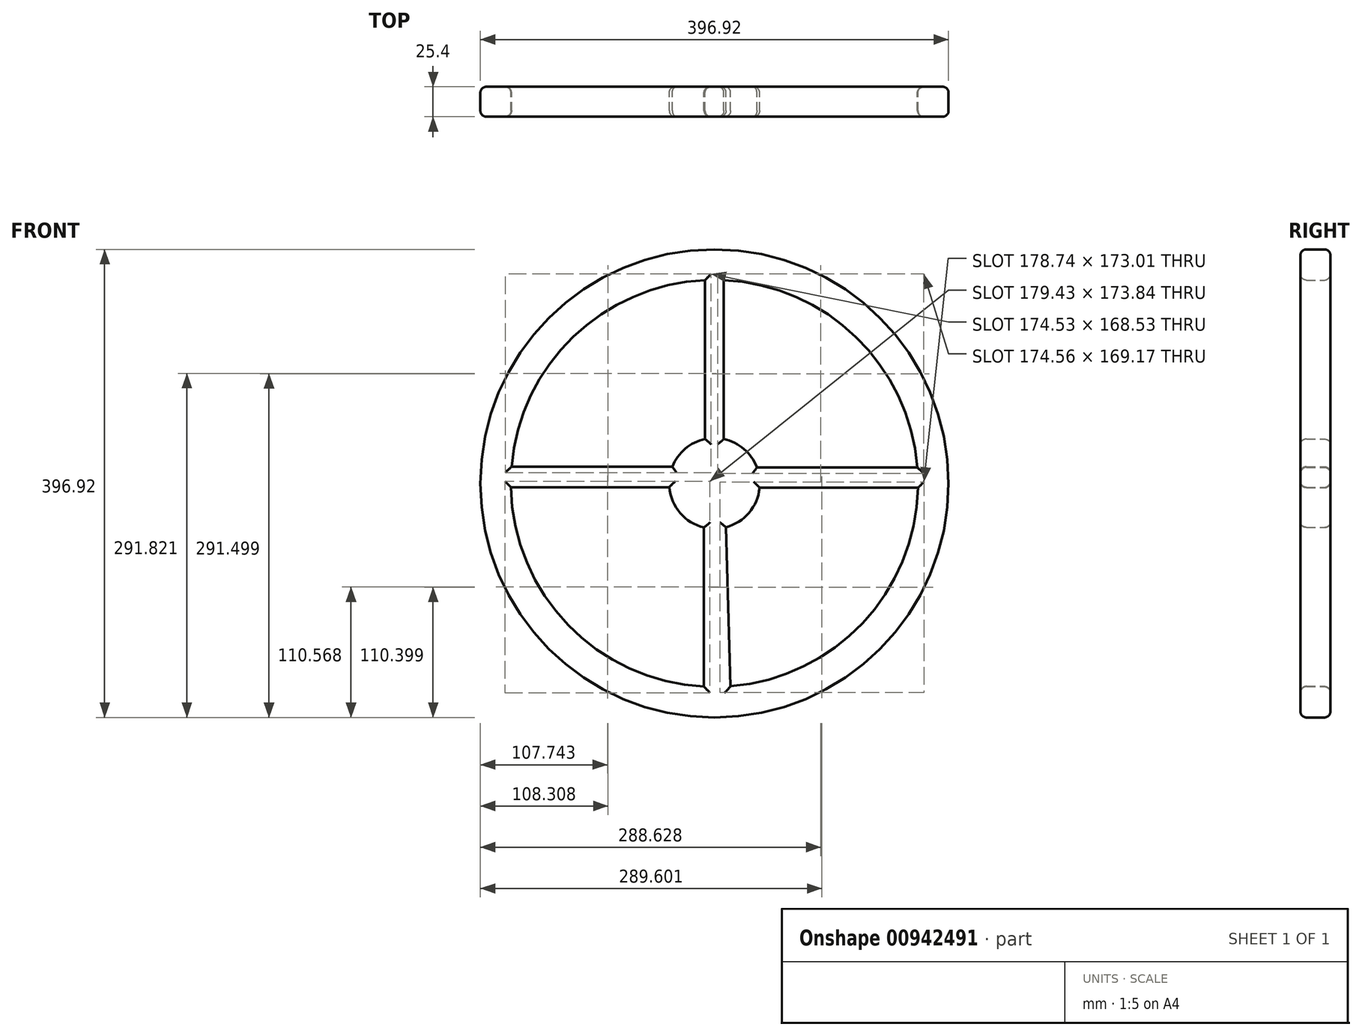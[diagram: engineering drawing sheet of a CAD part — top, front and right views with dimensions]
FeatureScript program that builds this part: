
annotation { "Feature Type Name" : "Feature", "Feature Type Description" : "" }
export const myFeature = defineFeature(function(context is Context, id is Id, definition is map)
    precondition{}
    {
        {
            var Q0;
            Q0=qCreatedBy(makeId("Front.planeOp"),FACE);
            var sketch = newSketch(context, id + "F0", { "sketchPlane" : qUnion([Q0])});
            skCircle(sketch, "E0", {"center": v(0, 0) * mm, "radius": 198.46 * mm});
            skCircle(sketch, "E1", {"center": v(0, 0) * mm, "radius": 172.57 * mm});
            skCircle(sketch, "E2", {"center": v(0, 0) * mm, "radius": 38.43 * mm});
            skLineSegment(sketch, "E3", {"start": v(-7.97, 172.38) * mm, "end": v(-7.97, 37.6) * mm});
            skLineSegment(sketch, "E4", {"start": v(7.97, 37.6) * mm, "end": v(7.97, 172.38) * mm});
            skLineSegment(sketch, "E5", {"start": v(-8.87, -37.4) * mm, "end": v(-8.87, -172.34) * mm});
            skLineSegment(sketch, "E6", {"start": v(9.84, -37.15) * mm, "end": v(13.69, -172.02) * mm});
            skLineSegment(sketch, "E7", {"start": v(-35.72, 14.18) * mm, "end": v(-171.98, 14.18) * mm});
            skLineSegment(sketch, "E8", {"start": v(-38.3, -3.26) * mm, "end": v(-172.54, -3.26) * mm});
            skLineSegment(sketch, "E9", {"start": v(35.97, 13.53) * mm, "end": v(172.04, 13.53) * mm});
            skLineSegment(sketch, "E10", {"start": v(38.24, -3.77) * mm, "end": v(172.53, -3.77) * mm});
            skSolve(sketch);
        }
        {
            var Q0;
            Q0=makeQuery(id+"F0.imprint","IMPRINT",FACE,{"disambiguationData":[TD([[makeQuery(id+"F0.imprint","IMPRINT",EDGE,{"derivedFrom":sQuery(id+"F0.wireOp",EDGE,"E0")}),1.0]])]});
            var Q1;
            {var subQ0=sQuery(id+"F0.wireOp",EDGE,"E3");Q1=makeQuery(id+"F0.imprint","IMPRINT",FACE,{"disambiguationData":[TD([[makeQuery(id+"F0.imprint","IMPRINT",EDGE,{"derivedFrom":subQ0}),1.0]])]});}
            var Q2;
            {var subQ0=sQuery(id+"F0.wireOp",EDGE,"E7");Q2=makeQuery(id+"F0.imprint","IMPRINT",FACE,{"disambiguationData":[TD([[makeQuery(id+"F0.imprint","IMPRINT",EDGE,{"derivedFrom":subQ0}),1.0]])]});}
            var Q3;
            {var subQ4=sQuery(id+"F0.wireOp",EDGE,"DAilxVQu-HEWN-SxXB-gtyP-NfDb4dbdtztd");Q3=makeQuery(id+"F0.imprint","IMPRINT",FACE,{"disambiguationData":[TD([[makeQuery(id+"F0.imprint","IMPRINT",EDGE,{"derivedFrom":subQ4}),-1.0]])]});}
            var Q4;
            {var subQ0=sQuery(id+"F0.wireOp",EDGE,"E9");Q4=makeQuery(id+"F0.imprint","IMPRINT",FACE,{"disambiguationData":[TD([[makeQuery(id+"F0.imprint","IMPRINT",EDGE,{"derivedFrom":subQ0}),-1.0]])]});}
            var Q5;
            {var subQ0=sQuery(id+"F0.wireOp",EDGE,"E5");Q5=makeQuery(id+"F0.imprint","IMPRINT",FACE,{"disambiguationData":[TD([[makeQuery(id+"F0.imprint","IMPRINT",EDGE,{"derivedFrom":subQ0}),1.0]])]});}
            var Q6;
            {var subQ0=sQuery(id+"F0.wireOp",EDGE,"E2");var subQ4=makeQuery(id+"F0.imprint","INTERSECT",VERTEX,{"derivedFrom":[subQ0,sQuery(id+"F0.wireOp",EDGE,"E4")]});Q6=makeQuery(id+"F0.imprint","IMPRINT",FACE,{"disambiguationData":[TD([[makeQuery(id+"F0.imprint","IMPRINT",EDGE,{"disambiguationData":[TD([[subQ4,1.0]])],"derivedFrom":subQ0}),1.0]])]});}
            extrude(context, id + "F1", {"entities" : qUnion([Q0, Q1, Q2, Q3, Q4, Q5, Q6]), "depth" : 25.4 * mm, "offsetDistance" : 25.4 * mm});
        }
        {
            var Q0;
            Q0=makeQuery(id+"F1.opExtrude","CAP_EDGE",EDGE,{"disambiguationData":[OSD([sQuery(id+"F0.wireOp",EDGE,"E0")])],"isStart":false});
            var Q1;
            {var subQ0=sQuery(id+"F0.wireOp",EDGE,"E1");Q1=makeQuery(id+"F1.opExtrude","CAP_EDGE",EDGE,{"disambiguationData":[OSD([subQ0]),TDD([makeQuery(id+"F0.imprint","IMPRINT",EDGE,{"disambiguationData":[TD([[makeQuery(id+"F0.imprint","INTERSECT",VERTEX,{"derivedFrom":[subQ0,sQuery(id+"F0.wireOp",EDGE,"E3")]}),-1.0]])],"derivedFrom":subQ0})])],"isStart":false});}
            var Q2;
            {var subQ0=sQuery(id+"F0.wireOp",EDGE,"E1");Q2=makeQuery(id+"F1.opExtrude","CAP_EDGE",EDGE,{"disambiguationData":[OSD([subQ0]),TDD([makeQuery(id+"F0.imprint","IMPRINT",EDGE,{"disambiguationData":[TD([[makeQuery(id+"F0.imprint","INTERSECT",VERTEX,{"derivedFrom":[subQ0,sQuery(id+"F0.wireOp",EDGE,"E4")]}),1.0]])],"derivedFrom":subQ0})])],"isStart":false});}
            var Q3;
            {var subQ0=sQuery(id+"F0.wireOp",EDGE,"E1");Q3=makeQuery(id+"F1.opExtrude","CAP_EDGE",EDGE,{"disambiguationData":[OSD([subQ0]),TDD([makeQuery(id+"F0.imprint","IMPRINT",EDGE,{"disambiguationData":[TD([[makeQuery(id+"F0.imprint","INTERSECT",VERTEX,{"derivedFrom":[subQ0,sQuery(id+"F0.wireOp",EDGE,"E6")]}),-1.0]])],"derivedFrom":subQ0})])],"isStart":false});}
            var Q4;
            {var subQ0=sQuery(id+"F0.wireOp",EDGE,"E1");Q4=makeQuery(id+"F1.opExtrude","CAP_EDGE",EDGE,{"disambiguationData":[OSD([subQ0]),TDD([makeQuery(id+"F0.imprint","IMPRINT",EDGE,{"disambiguationData":[TD([[makeQuery(id+"F0.imprint","INTERSECT",VERTEX,{"derivedFrom":[subQ0,sQuery(id+"F0.wireOp",EDGE,"E5")]}),1.0]])],"derivedFrom":subQ0})])],"isStart":false});}
            fillet(context, id + "F2", {"entities" : qUnion([Q0, Q1, Q2, Q3, Q4]), "radius" : 5.08 * mm, "tangentPropagation" : true, "allowEdgeOverflow" : false});
        }
        {
            var Q0;
            Q0=makeQuery(id+"F1.opExtrude","CAP_EDGE",EDGE,{"disambiguationData":[OSD([sQuery(id+"F0.wireOp",EDGE,"E0")])],"isStart":true});
            var Q1;
            {var subQ0=sQuery(id+"F0.wireOp",EDGE,"E1");Q1=makeQuery(id+"F1.opExtrude","CAP_EDGE",EDGE,{"disambiguationData":[OSD([subQ0]),TDD([makeQuery(id+"F0.imprint","IMPRINT",EDGE,{"disambiguationData":[TD([[makeQuery(id+"F0.imprint","INTERSECT",VERTEX,{"derivedFrom":[subQ0,sQuery(id+"F0.wireOp",EDGE,"E4")]}),1.0]])],"derivedFrom":subQ0})])],"isStart":true});}
            var Q2;
            {var subQ0=sQuery(id+"F0.wireOp",EDGE,"E1");Q2=makeQuery(id+"F1.opExtrude","CAP_EDGE",EDGE,{"disambiguationData":[OSD([subQ0]),TDD([makeQuery(id+"F0.imprint","IMPRINT",EDGE,{"disambiguationData":[TD([[makeQuery(id+"F0.imprint","INTERSECT",VERTEX,{"derivedFrom":[subQ0,sQuery(id+"F0.wireOp",EDGE,"E6")]}),-1.0]])],"derivedFrom":subQ0})])],"isStart":true});}
            var Q3;
            {var subQ0=sQuery(id+"F0.wireOp",EDGE,"E1");Q3=makeQuery(id+"F1.opExtrude","CAP_EDGE",EDGE,{"disambiguationData":[OSD([subQ0]),TDD([makeQuery(id+"F0.imprint","IMPRINT",EDGE,{"disambiguationData":[TD([[makeQuery(id+"F0.imprint","INTERSECT",VERTEX,{"derivedFrom":[subQ0,sQuery(id+"F0.wireOp",EDGE,"E3")]}),-1.0]])],"derivedFrom":subQ0})])],"isStart":true});}
            var Q4;
            {var subQ0=sQuery(id+"F0.wireOp",EDGE,"E1");Q4=makeQuery(id+"F1.opExtrude","CAP_EDGE",EDGE,{"disambiguationData":[OSD([subQ0]),TDD([makeQuery(id+"F0.imprint","IMPRINT",EDGE,{"disambiguationData":[TD([[makeQuery(id+"F0.imprint","INTERSECT",VERTEX,{"derivedFrom":[subQ0,sQuery(id+"F0.wireOp",EDGE,"E5")]}),1.0]])],"derivedFrom":subQ0})])],"isStart":true});}
            fillet(context, id + "F3", {"entities" : qUnion([Q0, Q1, Q2, Q3, Q4]), "radius" : 5.08 * mm, "tangentPropagation" : true, "allowEdgeOverflow" : false});
        }
        {
            var Q0;
            Q0=makeQuery(id+"F1.opExtrude","CAP_EDGE",EDGE,{"disambiguationData":[OSD([sQuery(id+"F0.wireOp",EDGE,"E3")])],"isStart":true});
            var Q1;
            Q1=makeQuery(id+"F1.opExtrude","CAP_EDGE",EDGE,{"disambiguationData":[OSD([sQuery(id+"F0.wireOp",EDGE,"E4")])],"isStart":false});
            var Q2;
            Q2=makeQuery(id+"F1.opExtrude","CAP_EDGE",EDGE,{"disambiguationData":[OSD([sQuery(id+"F0.wireOp",EDGE,"E4")])],"isStart":true});
            var Q3;
            Q3=makeQuery(id+"F1.opExtrude","CAP_EDGE",EDGE,{"disambiguationData":[OSD([sQuery(id+"F0.wireOp",EDGE,"E3")])],"isStart":false});
            fillet(context, id + "F4", {"entities" : qUnion([Q0, Q1, Q2, Q3]), "radius" : 5.08 * mm, "tangentPropagation" : true, "allowEdgeOverflow" : false});
        }
        {
            var Q0;
            Q0=makeQuery(id+"F1.opExtrude","CAP_EDGE",EDGE,{"disambiguationData":[OSD([sQuery(id+"F0.wireOp",EDGE,"E10")])],"isStart":true});
            var Q1;
            Q1=makeQuery(id+"F1.opExtrude","CAP_EDGE",EDGE,{"disambiguationData":[OSD([sQuery(id+"F0.wireOp",EDGE,"E9")])],"isStart":true});
            var Q2;
            Q2=makeQuery(id+"F1.opExtrude","CAP_EDGE",EDGE,{"disambiguationData":[OSD([sQuery(id+"F0.wireOp",EDGE,"E9")])],"isStart":false});
            var Q3;
            Q3=makeQuery(id+"F1.opExtrude","CAP_EDGE",EDGE,{"disambiguationData":[OSD([sQuery(id+"F0.wireOp",EDGE,"E10")])],"isStart":false});
            fillet(context, id + "F5", {"entities" : qUnion([Q0, Q1, Q2, Q3]), "radius" : 5.08 * mm, "tangentPropagation" : true, "allowEdgeOverflow" : false});
        }
        {
            var Q0;
            Q0=makeQuery(id+"F1.opExtrude","CAP_EDGE",EDGE,{"disambiguationData":[OSD([sQuery(id+"F0.wireOp",EDGE,"E6")])],"isStart":true});
            var Q1;
            Q1=makeQuery(id+"F1.opExtrude","CAP_EDGE",EDGE,{"disambiguationData":[OSD([sQuery(id+"F0.wireOp",EDGE,"E5")])],"isStart":true});
            var Q2;
            Q2=makeQuery(id+"F1.opExtrude","CAP_EDGE",EDGE,{"disambiguationData":[OSD([sQuery(id+"F0.wireOp",EDGE,"E6")])],"isStart":false});
            var Q3;
            Q3=makeQuery(id+"F1.opExtrude","CAP_EDGE",EDGE,{"disambiguationData":[OSD([sQuery(id+"F0.wireOp",EDGE,"E5")])],"isStart":false});
            fillet(context, id + "F6", {"entities" : qUnion([Q0, Q1, Q2, Q3]), "radius" : 5.08 * mm, "tangentPropagation" : true, "allowEdgeOverflow" : false});
        }
        {
            var Q0;
            Q0=makeQuery(id+"F1.opExtrude","CAP_EDGE",EDGE,{"disambiguationData":[OSD([sQuery(id+"F0.wireOp",EDGE,"E7")])],"isStart":false});
            var Q1;
            Q1=makeQuery(id+"F1.opExtrude","CAP_EDGE",EDGE,{"disambiguationData":[OSD([sQuery(id+"F0.wireOp",EDGE,"E8")])],"isStart":false});
            var Q2;
            Q2=makeQuery(id+"F1.opExtrude","CAP_EDGE",EDGE,{"disambiguationData":[OSD([sQuery(id+"F0.wireOp",EDGE,"E8")])],"isStart":true});
            var Q3;
            Q3=makeQuery(id+"F1.opExtrude","CAP_EDGE",EDGE,{"disambiguationData":[OSD([sQuery(id+"F0.wireOp",EDGE,"E7")])],"isStart":true});
            fillet(context, id + "F7", {"entities" : qUnion([Q0, Q1, Q2, Q3]), "radius" : 5.08 * mm, "tangentPropagation" : true, "allowEdgeOverflow" : false});
        }
        {
            var Q0;
            {var subQ0=sQuery(id+"F0.wireOp",EDGE,"E2");Q0=makeQuery(id+"F1.opExtrude","CAP_EDGE",EDGE,{"disambiguationData":[OSD([subQ0]),TDD([makeQuery(id+"F0.imprint","IMPRINT",EDGE,{"disambiguationData":[TD([[makeQuery(id+"F0.imprint","INTERSECT",VERTEX,{"derivedFrom":[subQ0,sQuery(id+"F0.wireOp",EDGE,"E4")]}),1.0]])],"derivedFrom":subQ0})])],"isStart":false});}
            var Q1;
            {var subQ0=sQuery(id+"F0.wireOp",EDGE,"E2");Q1=makeQuery(id+"F1.opExtrude","CAP_EDGE",EDGE,{"disambiguationData":[OSD([subQ0]),TDD([makeQuery(id+"F0.imprint","IMPRINT",EDGE,{"disambiguationData":[TD([[makeQuery(id+"F0.imprint","INTERSECT",VERTEX,{"derivedFrom":[subQ0,sQuery(id+"F0.wireOp",EDGE,"E4")]}),1.0]])],"derivedFrom":subQ0})])],"isStart":true});}
            var Q2;
            {var subQ0=sQuery(id+"F0.wireOp",EDGE,"E2");Q2=makeQuery(id+"F1.opExtrude","CAP_EDGE",EDGE,{"disambiguationData":[OSD([subQ0]),TDD([makeQuery(id+"F0.imprint","IMPRINT",EDGE,{"disambiguationData":[TD([[makeQuery(id+"F0.imprint","INTERSECT",VERTEX,{"derivedFrom":[subQ0,sQuery(id+"F0.wireOp",EDGE,"E6")]}),-1.0]])],"derivedFrom":subQ0})])],"isStart":false});}
            var Q3;
            {var subQ0=sQuery(id+"F0.wireOp",EDGE,"E2");Q3=makeQuery(id+"F1.opExtrude","CAP_EDGE",EDGE,{"disambiguationData":[OSD([subQ0]),TDD([makeQuery(id+"F0.imprint","IMPRINT",EDGE,{"disambiguationData":[TD([[makeQuery(id+"F0.imprint","INTERSECT",VERTEX,{"derivedFrom":[subQ0,sQuery(id+"F0.wireOp",EDGE,"E6")]}),-1.0]])],"derivedFrom":subQ0})])],"isStart":true});}
            var Q4;
            {var subQ0=sQuery(id+"F0.wireOp",EDGE,"E2");Q4=makeQuery(id+"F1.opExtrude","CAP_EDGE",EDGE,{"disambiguationData":[OSD([subQ0]),TDD([makeQuery(id+"F0.imprint","IMPRINT",EDGE,{"disambiguationData":[TD([[makeQuery(id+"F0.imprint","INTERSECT",VERTEX,{"derivedFrom":[subQ0,sQuery(id+"F0.wireOp",EDGE,"E3")]}),-1.0]])],"derivedFrom":subQ0})])],"isStart":false});}
            var Q5;
            {var subQ0=sQuery(id+"F0.wireOp",EDGE,"E2");Q5=makeQuery(id+"F1.opExtrude","CAP_EDGE",EDGE,{"disambiguationData":[OSD([subQ0]),TDD([makeQuery(id+"F0.imprint","IMPRINT",EDGE,{"disambiguationData":[TD([[makeQuery(id+"F0.imprint","INTERSECT",VERTEX,{"derivedFrom":[subQ0,sQuery(id+"F0.wireOp",EDGE,"E3")]}),-1.0]])],"derivedFrom":subQ0})])],"isStart":true});}
            var Q6;
            {var subQ0=sQuery(id+"F0.wireOp",EDGE,"E2");Q6=makeQuery(id+"F1.opExtrude","CAP_EDGE",EDGE,{"disambiguationData":[OSD([subQ0]),TDD([makeQuery(id+"F0.imprint","IMPRINT",EDGE,{"disambiguationData":[TD([[makeQuery(id+"F0.imprint","INTERSECT",VERTEX,{"derivedFrom":[subQ0,sQuery(id+"F0.wireOp",EDGE,"E5")]}),1.0]])],"derivedFrom":subQ0})])],"isStart":true});}
            var Q7;
            {var subQ0=sQuery(id+"F0.wireOp",EDGE,"E2");Q7=makeQuery(id+"F1.opExtrude","CAP_EDGE",EDGE,{"disambiguationData":[OSD([subQ0]),TDD([makeQuery(id+"F0.imprint","IMPRINT",EDGE,{"disambiguationData":[TD([[makeQuery(id+"F0.imprint","INTERSECT",VERTEX,{"derivedFrom":[subQ0,sQuery(id+"F0.wireOp",EDGE,"E5")]}),1.0]])],"derivedFrom":subQ0})])],"isStart":false});}
            fillet(context, id + "F8", {"entities" : qUnion([Q0, Q1, Q2, Q3, Q4, Q5, Q6, Q7]), "radius" : 5.08 * mm, "tangentPropagation" : true, "allowEdgeOverflow" : false});
        }
    });
